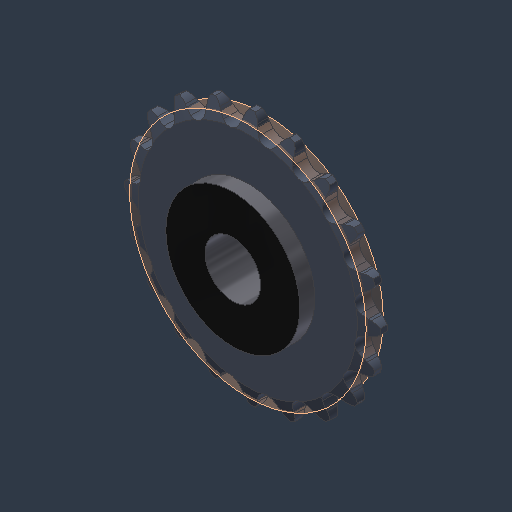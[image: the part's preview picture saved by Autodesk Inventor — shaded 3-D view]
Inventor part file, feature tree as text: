
AUTODESK INVENTOR PART (.ipt)
format: ipt  version: 2024.3 (Build 283343000, 343)  size: 604,672 bytes
history: native  units: mm (DEFAULTED — no unit token found)
features: plane x2, other x2, sketch x1, extrude x1
ambient origin geometry x8: Origin, YZ Plane, XZ Plane, XY Plane, X Axis, Y Axis, Z Axis, Center Point
bodies: Solid1 (feature_tree)
feature tree (6):
  plane  "Work Plane1"
  sketch  "Sketch2"  dims[d0=40.5892mm d1=25.4mm d2=0.0mm]
  plane  "Work Plane2"
  other  "Srf1"
  other  "Cut-Extrude2"
  extrude  "ExtrusionSrf1"  Depth=25.4mm TaperAngle=0.0deg
